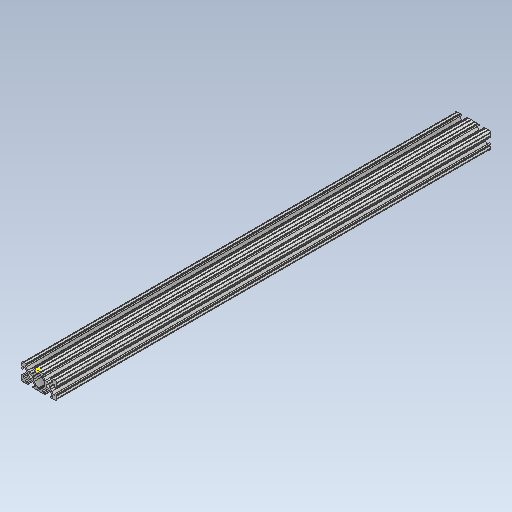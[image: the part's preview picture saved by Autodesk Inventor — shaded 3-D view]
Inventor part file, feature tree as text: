
AUTODESK INVENTOR PART (.ipt)
format: ipt  version: 2020 (Build 240168000, 168)  size: 382,976 bytes
history: native  units: in
note: dims shown in document units (in); Inventor stores cm internally (conversion verified against a paired STEP export)
features: other x3, sketch x2
ambient origin geometry x8: Origin, YZ Plane, XZ Plane, XY Plane, X Axis, Y Axis, Z Axis, Center Point
bodies: Solid1 (feature_tree)
feature tree (5):
  other  "25in 2x1 T Slot.ipt"
  other  "Solid1::25in 2x1 T Slot.ipt"
  other  "TaggingFeature1"
  sketch  "Sketch1"  dims[d0=0.3937in]
  sketch  "Sketch2"
